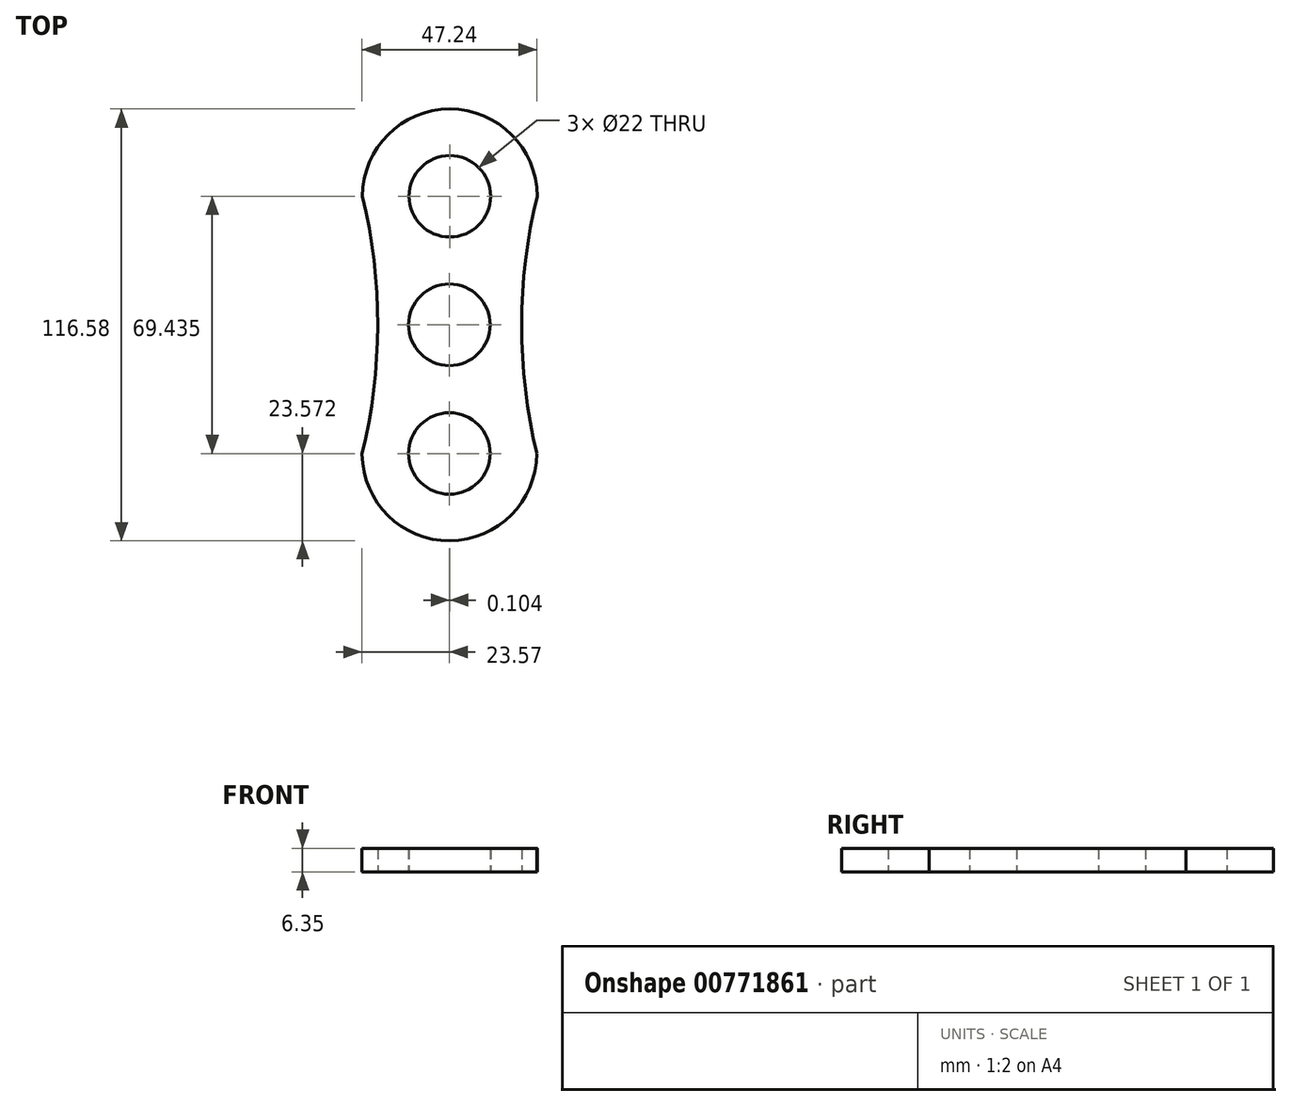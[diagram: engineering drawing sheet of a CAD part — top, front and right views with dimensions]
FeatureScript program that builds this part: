
annotation { "Feature Type Name" : "Feature", "Feature Type Description" : "" }
export const myFeature = defineFeature(function(context is Context, id is Id, definition is map)
    precondition{}
    {
        {
            var Q0;
            Q0=qCreatedBy(makeId("Top.planeOp"),FACE);
            var sketch = newSketch(context, id + "F0", { "sketchPlane" : qUnion([Q0])});
            skCircle(sketch, "E0", {"center": v(0, 0) * mm, "radius": 11 * mm});
            skCircle(sketch, "E1", {"center": v(0.1, 34.7) * mm, "radius": 11 * mm});
            skCircle(sketch, "E2", {"center": v(0, -34.73) * mm, "radius": 11 * mm});
            skArc(sketch, "E3", {"start": v(23.67, 34.7) * mm, "mid": v(19.5, 0) * mm, "end": v(23.57, -34.73) * mm});
            skArc(sketch, "E4.trimOffspring", {"start": v(23.67, 34.7) * mm, "mid": v(0.1, 58.28) * mm, "end": v(-23.47, 34.7) * mm});
            skArc(sketch, "E5", {"start": v(-23.57, -34.98) * mm, "mid": v(-19.37, -0.14) * mm, "end": v(-23.47, 34.7) * mm});
            skArc(sketch, "E6.trimOffspring", {"start": v(-23.57, -34.98) * mm, "mid": v(0.12, -58.3) * mm, "end": v(23.57, -34.73) * mm});
            skSolve(sketch);
        }
        {
            var Q0;
            {var subQ0=sQuery(id+"F0.wireOp",EDGE,"23IeSJm8-HUYG-KUZd-2Etc-yxjgn8sEN3bH");Q0=makeQuery(id+"F0.imprint","IMPRINT",FACE,{"disambiguationData":[TD([[makeQuery(id+"F0.imprint","IMPRINT",EDGE,{"derivedFrom":subQ0}),1.0]])]});}
            var Q1;
            {var subQ3=sQuery(id+"F0.wireOp",EDGE,"vE4nXrlW-LjaM-8Q0j-uKgn-IrhpBW9p9us6");var subQ5=sQuery(id+"F0.wireOp",EDGE,"E0");var subQ6=makeQuery(id+"F0.imprint","INTERSECT",VERTEX,{"derivedFrom":[subQ5,subQ3]});Q1=makeQuery(id+"F0.imprint","IMPRINT",FACE,{"disambiguationData":[TD([[makeQuery(id+"F0.imprint","IMPRINT",EDGE,{"disambiguationData":[TD([[subQ6,-1.0]])],"derivedFrom":subQ5}),-1.0]])]});}
            var Q2;
            Q2=makeQuery(id+"F0.imprint","IMPRINT",FACE,{"disambiguationData":[TD([[makeQuery(id+"F0.imprint","IMPRINT",EDGE,{"derivedFrom":sQuery(id+"F0.wireOp",EDGE,"E1")}),-1.0]])]});
            var Q3;
            Q3=makeQuery(id+"F0.imprint","IMPRINT",FACE,{"disambiguationData":[TD([[makeQuery(id+"F0.imprint","IMPRINT",EDGE,{"derivedFrom":sQuery(id+"F0.wireOp",EDGE,"E2")}),-1.0]])]});
            extrude(context, id + "F1", {"entities" : qUnion([Q0, Q1, Q2, Q3]), "depth" : 6.35 * mm, "offsetDistance" : 25.4 * mm});
        }
    });
